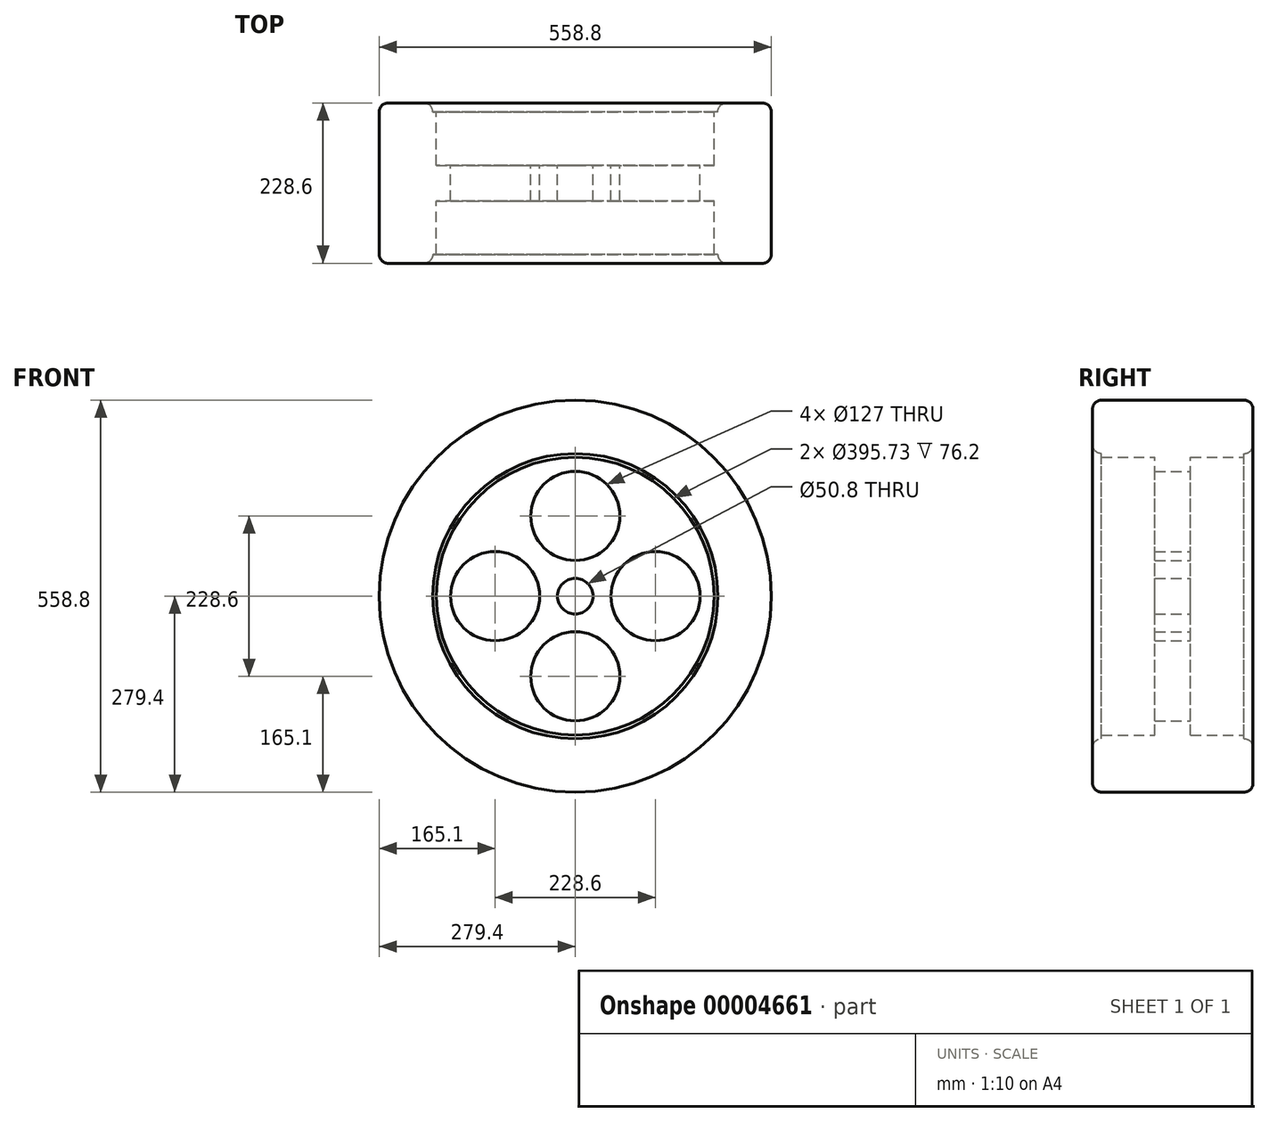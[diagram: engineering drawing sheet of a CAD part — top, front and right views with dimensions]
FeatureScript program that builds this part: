
annotation { "Feature Type Name" : "Feature", "Feature Type Description" : "" }
export const myFeature = defineFeature(function(context is Context, id is Id, definition is map)
    precondition{}
    {
        {
            var Q0;
            Q0=qCreatedBy(makeId("Front.planeOp"),FACE);
            var sketch = newSketch(context, id + "F0", { "sketchPlane" : qUnion([Q0])});
            skCircle(sketch, "E0", {"center": v(0, 0) * mm, "radius": 279.4 * mm});
            skCircle(sketch, "E1", {"center": v(0, 0) * mm, "radius": 203.2 * mm});
            skCircle(sketch, "E2", {"center": v(0, 0) * mm, "radius": 114.3 * mm, "construction": true});
            skLineSegment(sketch, "E3", {"start": v(0, 0) * mm, "end": v(-511.16, 0) * mm, "construction": true});
            skLineSegment(sketch, "E4", {"start": v(0, 0) * mm, "end": v(394.12, 0) * mm, "construction": true});
            skLineSegment(sketch, "E5", {"start": v(0, 0) * mm, "end": v(0, 354.47) * mm, "construction": true});
            skLineSegment(sketch, "E6", {"start": v(0, 0) * mm, "end": v(0, -279.4) * mm, "construction": true});
            skCircle(sketch, "E7", {"center": v(-114.3, 0) * mm, "radius": 63.5 * mm});
            skCircle(sketch, "E8", {"center": v(114.3, 0) * mm, "radius": 63.5 * mm});
            skCircle(sketch, "E9", {"center": v(0, -114.3) * mm, "radius": 63.5 * mm});
            skCircle(sketch, "E10", {"center": v(0, 114.3) * mm, "radius": 63.5 * mm});
            skCircle(sketch, "E11", {"center": v(0, 0) * mm, "radius": 25.4 * mm});
            skCircle(sketch, "E12", {"center": v(0, 0) * mm, "radius": 197.87 * mm});
            skSolve(sketch);
        }
        {
            var Q0;
            Q0=makeQuery(id+"F0.imprint","IMPRINT",FACE,{"disambiguationData":[TD([[makeQuery(id+"F0.imprint","IMPRINT",EDGE,{"derivedFrom":sQuery(id+"F0.wireOp",EDGE,"E7")}),-1.0]])]});
            extrude(context, id + "F1", {"entities" : qUnion([Q0]), "endBound" : BoundingType.SYMMETRIC, "depth" : 50.8 * mm});
        }
        {
            var Q0;
            Q0=makeQuery(id+"F0.imprint","IMPRINT",FACE,{"disambiguationData":[TD([[makeQuery(id+"F0.imprint","IMPRINT",EDGE,{"derivedFrom":sQuery(id+"F0.wireOp",EDGE,"E0")}),1.0]])]});
            extrude(context, id + "F2", {"entities" : qUnion([Q0]), "endBound" : BoundingType.SYMMETRIC, "depth" : 228.6 * mm});
        }
        {
            var Q0;
            Q0=makeQuery(id+"F2.opExtrude","CAP_EDGE",EDGE,{"disambiguationData":[OSD([sQuery(id+"F0.wireOp",EDGE,"E0")])],"isStart":false});
            var Q1;
            Q1=makeQuery(id+"F2.opExtrude","CAP_EDGE",EDGE,{"disambiguationData":[OSD([sQuery(id+"F0.wireOp",EDGE,"E1")])],"isStart":false});
            fillet(context, id + "F3", {"entities" : qUnion([Q0, Q1]), "radius" : 12.7 * mm, "tangentPropagation" : true, "allowEdgeOverflow" : false});
        }
        {
            var Q0;
            Q0=makeQuery(id+"F2.opExtrude","CAP_EDGE",EDGE,{"disambiguationData":[OSD([sQuery(id+"F0.wireOp",EDGE,"E0")])],"isStart":true});
            var Q1;
            Q1=makeQuery(id+"F2.opExtrude","CAP_EDGE",EDGE,{"disambiguationData":[OSD([sQuery(id+"F0.wireOp",EDGE,"E1")])],"isStart":true});
            fillet(context, id + "F4", {"entities" : qUnion([Q0, Q1]), "radius" : 12.7 * mm, "tangentPropagation" : true, "allowEdgeOverflow" : false});
        }
        {
            var Q0;
            Q0=makeQuery(id+"F0.imprint","IMPRINT",FACE,{"disambiguationData":[TD([[makeQuery(id+"F0.imprint","IMPRINT",EDGE,{"derivedFrom":sQuery(id+"F0.wireOp",EDGE,"E12")}),-1.0]])]});
            extrude(context, id + "F5", {"entities" : qUnion([Q0]), "operationType" : NewBodyOperationType.ADD, "endBound" : BoundingType.SYMMETRIC, "depth" : 203.2 * mm});
        }
    });
